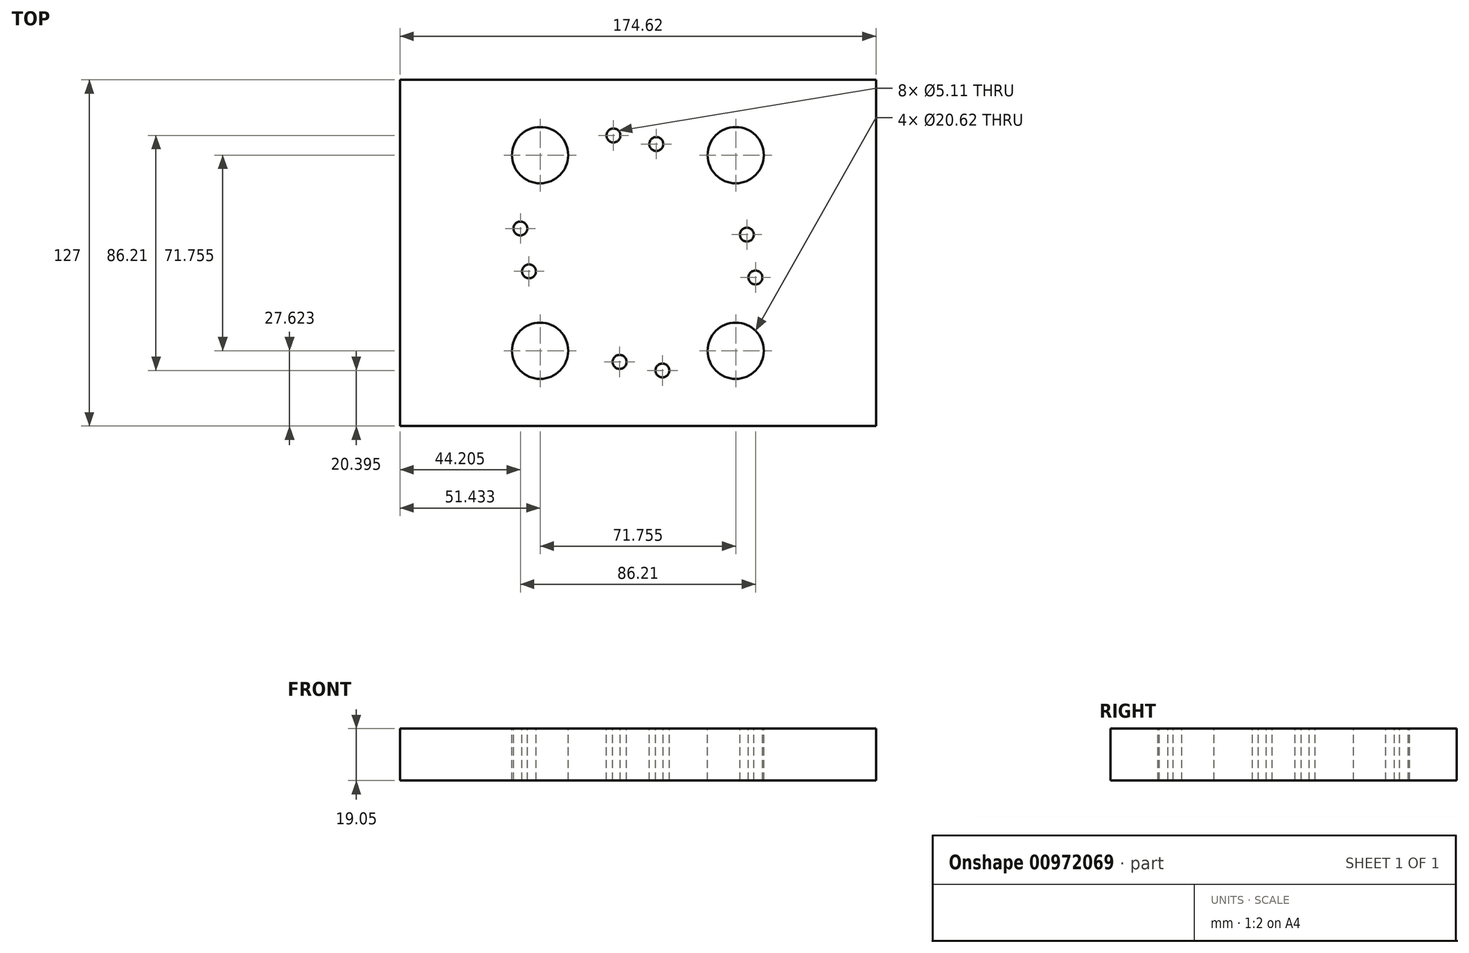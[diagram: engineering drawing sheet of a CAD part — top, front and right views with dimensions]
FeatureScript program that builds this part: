
annotation { "Feature Type Name" : "Feature", "Feature Type Description" : "" }
export const myFeature = defineFeature(function(context is Context, id is Id, definition is map)
    precondition{}
    {
        {
            var Q0;
            Q0=qCreatedBy(makeId("Top.planeOp"),FACE);
            var sketch = newSketch(context, id + "F0", { "sketchPlane" : qUnion([Q0])});
            skLineSegment(sketch, "E0.bottom", {"start": v(87.31, -63.5) * mm, "end": v(-87.31, -63.5) * mm});
            skLineSegment(sketch, "E0.top", {"start": v(87.31, 63.5) * mm, "end": v(-87.31, 63.5) * mm});
            skLineSegment(sketch, "E0.left", {"start": v(87.31, -63.5) * mm, "end": v(87.31, 63.5) * mm});
            skLineSegment(sketch, "E0.right", {"start": v(-87.31, -63.5) * mm, "end": v(-87.31, 63.5) * mm});
            skPoint(sketch, "E0.middle", {"position": v(0, 0) * mm});
            skSolve(sketch);
        }
        {
            var Q0;
            Q0=makeQuery(id+"F0.imprint","IMPRINT",FACE,{"disambiguationData":[TD([[makeQuery(id+"F0.imprint","IMPRINT",EDGE,{"derivedFrom":sQuery(id+"F0.wireOp",EDGE,"E0.bottom")}),-1.0]])]});
            extrude(context, id + "F1", {"entities" : qUnion([Q0]), "depth" : 19.05 * mm, "offsetDistance" : 25.4 * mm});
        }
        {
            var Q0;
            Q0=makeQuery(id+"F1.opExtrude","CAP_FACE",FACE,{"disambiguationData":[OSD([sQuery(id+"F0.wireOp",EDGE,"E0.bottom"),sQuery(id+"F0.wireOp",EDGE,"E0.top"),sQuery(id+"F0.wireOp",EDGE,"E0.left"),sQuery(id+"F0.wireOp",EDGE,"E0.right")])],"isStart":false});
            var sketch = newSketch(context, id + "F2", { "sketchPlane" : qUnion([Q0])});
            skLineSegment(sketch, "E1.bottom", {"start": v(35.88, -35.88) * mm, "end": v(-35.88, -35.88) * mm, "construction": true});
            skLineSegment(sketch, "E1.top", {"start": v(35.88, 35.88) * mm, "end": v(-35.88, 35.88) * mm, "construction": true});
            skLineSegment(sketch, "E1.left", {"start": v(35.88, -35.88) * mm, "end": v(35.88, 35.88) * mm, "construction": true});
            skLineSegment(sketch, "E1.right", {"start": v(-35.88, -35.88) * mm, "end": v(-35.88, 35.88) * mm, "construction": true});
            skPoint(sketch, "E1.middle", {"position": v(0, 0) * mm});
            skSolve(sketch);
        }
        {
            var Q0;
            Q0=sQuery(id+"F2.wireOp",VERTEX,"E1.top.end");
            var Q1;
            Q1=sQuery(id+"F2.wireOp",VERTEX,"E1.bottom.end");
            var Q2;
            Q2=sQuery(id+"F2.wireOp",VERTEX,"E1.top.start");
            var Q3;
            Q3=sQuery(id+"F2.wireOp",VERTEX,"E1.bottom.start");
            var Q4;
            Q4=makeQuery(id+"F1.opExtrude","SWEPT_BODY",BODY,{"disambiguationData":[OSD([sQuery(id+"F0.wireOp",EDGE,"E0.bottom"),sQuery(id+"F0.wireOp",EDGE,"E0.top"),sQuery(id+"F0.wireOp",EDGE,"E0.left"),sQuery(id+"F0.wireOp",EDGE,"E0.right")])]});
            hole(context, id + "F3", {"style" : HoleStyle.SIMPLE, "endStyle" : HoleEndStyle.THROUGH, "standardTappedOrClearance" : lookupTablePath({ "fit" : "Normal (ASME)", "standard" : "ANSI", "size" : "3/4", "type" : "Clearance" }), "standardBlindInLast" : lookupTablePath({ "fit" : "Normal", "standard" : "ANSI", "engagement" : "75%", "pitch" : "10 tpi", "size" : "3/4", "type" : "Clearance & tapped" }), "holeDiameter" : 20.62 * mm, "majorDiameter" : 6.35 * mm, "isTappedThrough" : true, "tappedDepth" : 12.7 * mm, "tapClearance" : 3, "startFromSketch" : true, "locations" : qUnion([Q0, Q1, Q2, Q3]), "scope" : qUnion([Q4])});
        }
        {
            var Q0;
            Q0=makeQuery(id+"F1.opExtrude","CAP_FACE",FACE,{"disambiguationData":[OSD([sQuery(id+"F0.wireOp",EDGE,"E0.bottom"),sQuery(id+"F0.wireOp",EDGE,"E0.top"),sQuery(id+"F0.wireOp",EDGE,"E0.left"),sQuery(id+"F0.wireOp",EDGE,"E0.right")])],"isStart":false});
            var sketch = newSketch(context, id + "F4", { "sketchPlane" : qUnion([Q0])});
            skPoint(sketch, "E2.middle", {"position": v(0, 0) * mm});
            skLineSegment(sketch, "E3.1.0", {"start": v(6.74, 39.96) * mm, "end": v(39.96, 6.74) * mm});
            skLineSegment(sketch, "E3.1.1", {"start": v(-43.1, 8.98) * mm, "end": v(-8.98, 43.1) * mm});
            skLineSegment(sketch, "E3.1.2", {"start": v(39.96, 6.74) * mm, "end": v(-6.74, -39.96) * mm});
            skLineSegment(sketch, "E3.1.3", {"start": v(8.98, -43.1) * mm, "end": v(-43.1, 8.98) * mm});
            skLineSegment(sketch, "E4", {"start": v(6.74, 39.96) * mm, "end": v(-39.96, -6.74) * mm});
            skLineSegment(sketch, "E5", {"start": v(-39.96, -6.74) * mm, "end": v(-6.74, -39.96) * mm});
            skLineSegment(sketch, "E6", {"start": v(-8.98, 43.1) * mm, "end": v(43.1, -8.98) * mm});
            skLineSegment(sketch, "E7", {"start": v(43.1, -8.98) * mm, "end": v(8.98, -43.1) * mm});
            skCircle(sketch, "E8.0", {"center": v(-35.88, 35.88) * mm, "radius": 10.31 * mm, "construction": true});
            skCircle(sketch, "E8.1", {"center": v(35.88, -35.88) * mm, "radius": 10.31 * mm, "construction": true});
            skLineSegment(sketch, "E9", {"start": v(-35.88, 35.88) * mm, "end": v(35.88, -35.88) * mm, "construction": true});
            skSolve(sketch);
        }
        {
            var Q0;
            Q0=sQuery(id+"F4.wireOp",VERTEX,"E3.1.1.end");
            var Q1;
            Q1=sQuery(id+"F4.wireOp",VERTEX,"E3.1.0.start");
            var Q2;
            Q2=sQuery(id+"F4.wireOp",VERTEX,"E3.1.1.start");
            var Q3;
            Q3=sQuery(id+"F4.wireOp",VERTEX,"E4.end");
            var Q4;
            Q4=sQuery(id+"F4.wireOp",VERTEX,"E3.1.2.end");
            var Q5;
            Q5=sQuery(id+"F4.wireOp",VERTEX,"E3.1.3.start");
            var Q6;
            Q6=sQuery(id+"F4.wireOp",VERTEX,"E6.end");
            var Q7;
            Q7=sQuery(id+"F4.wireOp",VERTEX,"E3.1.0.end");
            var Q8;
            Q8=makeQuery(id+"F1.opExtrude","SWEPT_BODY",BODY,{"disambiguationData":[OSD([sQuery(id+"F0.wireOp",EDGE,"E0.bottom"),sQuery(id+"F0.wireOp",EDGE,"E0.top"),sQuery(id+"F0.wireOp",EDGE,"E0.left"),sQuery(id+"F0.wireOp",EDGE,"E0.right")])]});
            hole(context, id + "F5", {"style" : HoleStyle.SIMPLE, "endStyle" : HoleEndStyle.THROUGH, "standardTappedOrClearance" : lookupTablePath({ "standard" : "ANSI", "engagement" : "75%", "pitch" : "20 tpi", "size" : "1/4", "type" : "Tapped" }), "standardBlindInLast" : lookupTablePath({ "standard" : "ANSI", "fit" : "Normal", "engagement" : "75%", "pitch" : "20 tpi", "size" : "1/4", "type" : "Clearance & tapped" }), "holeDiameter" : 5.1 * mm, "majorDiameter" : 6.35 * mm, "showTappedDepth" : true, "isTappedThrough" : true, "tappedDepth" : 12.7 * mm, "tapClearance" : 3, "startFromSketch" : true, "locations" : qUnion([Q0, Q1, Q2, Q3, Q4, Q5, Q6, Q7]), "scope" : qUnion([Q8])});
        }
    });
